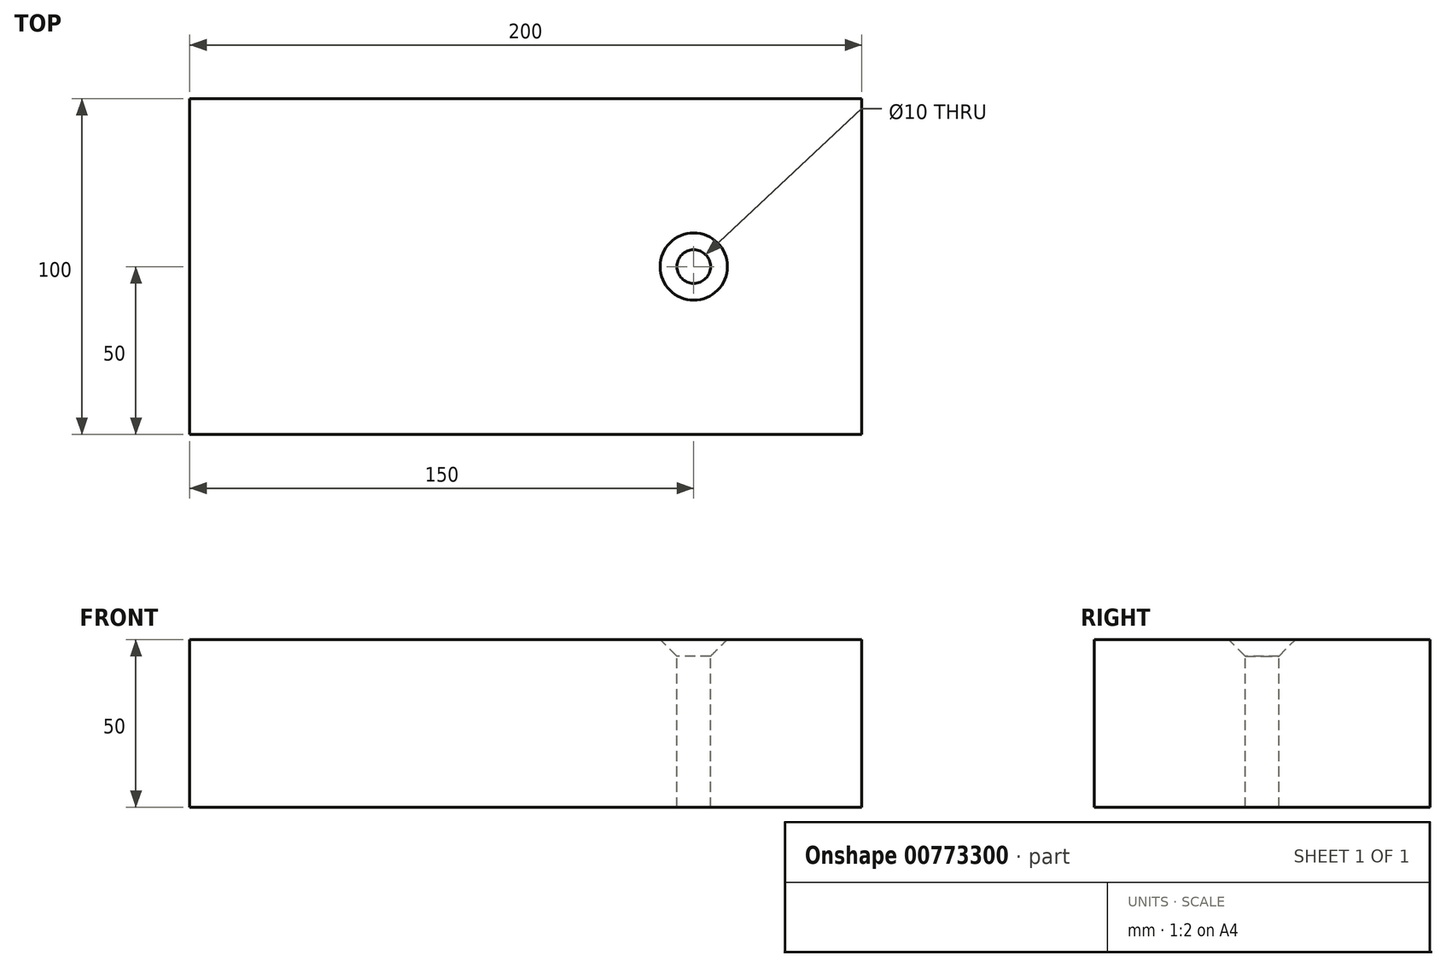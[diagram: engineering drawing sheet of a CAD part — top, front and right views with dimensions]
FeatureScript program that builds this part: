
annotation { "Feature Type Name" : "Feature", "Feature Type Description" : "" }
export const myFeature = defineFeature(function(context is Context, id is Id, definition is map)
    precondition{}
    {
        {
            var Q0;
            Q0=qCreatedBy(makeId("Top.planeOp"),FACE);
            var sketch = newSketch(context, id + "F0", { "sketchPlane" : qUnion([Q0])});
            skLineSegment(sketch, "E0.bottom", {"start": v(0, 0) * mm, "end": v(200, 0) * mm});
            skLineSegment(sketch, "E0.top", {"start": v(0, 100) * mm, "end": v(200, 100) * mm});
            skLineSegment(sketch, "E0.left", {"start": v(0, 0) * mm, "end": v(0, 100) * mm});
            skLineSegment(sketch, "E0.right", {"start": v(200, 0) * mm, "end": v(200, 100) * mm});
            skSolve(sketch);
        }
        {
            var Q0;
            Q0=makeQuery(id+"F0.imprint","IMPRINT",FACE,{"disambiguationData":[TD([[makeQuery(id+"F0.imprint","IMPRINT",EDGE,{"derivedFrom":sQuery(id+"F0.wireOp",EDGE,"E0.bottom")}),1.0]])]});
            extrude(context, id + "F1", {"entities" : qUnion([Q0]), "depth" : 50 * mm, "offsetDistance" : 25 * mm});
        }
        {
            var Q0;
            Q0=makeQuery(id+"F1.opExtrude","CAP_FACE",FACE,{"disambiguationData":[OSD([sQuery(id+"F0.wireOp",EDGE,"E0.bottom"),sQuery(id+"F0.wireOp",EDGE,"E0.top"),sQuery(id+"F0.wireOp",EDGE,"E0.left"),sQuery(id+"F0.wireOp",EDGE,"E0.right")])],"isStart":false});
            var sketch = newSketch(context, id + "F2", { "sketchPlane" : qUnion([Q0])});
            skPoint(sketch, "E1", {"position": v(150, 50) * mm});
            skSolve(sketch);
        }
        {
            var Q0;
            Q0=sQuery(id+"F2.wireOp",VERTEX,"E1");
            var Q1;
            Q1=makeQuery(id+"F1.opExtrude","SWEPT_BODY",BODY,{"disambiguationData":[OSD([sQuery(id+"F0.wireOp",EDGE,"E0.bottom"),sQuery(id+"F0.wireOp",EDGE,"E0.top"),sQuery(id+"F0.wireOp",EDGE,"E0.left"),sQuery(id+"F0.wireOp",EDGE,"E0.right")])]});
            hole(context, id + "F3", {"style" : HoleStyle.C_SINK, "endStyle" : HoleEndStyle.THROUGH, "holeDiameter" : 10 * mm, "cSinkDiameter" : 20 * mm, "cSinkAngle" : 90 * degree, "majorDiameter" : 5 * mm, "isTappedThrough" : true, "tappedDepth" : 12 * mm, "tapClearance" : 3, "locations" : qUnion([Q0]), "scope" : qUnion([Q1])});
        }
    });
